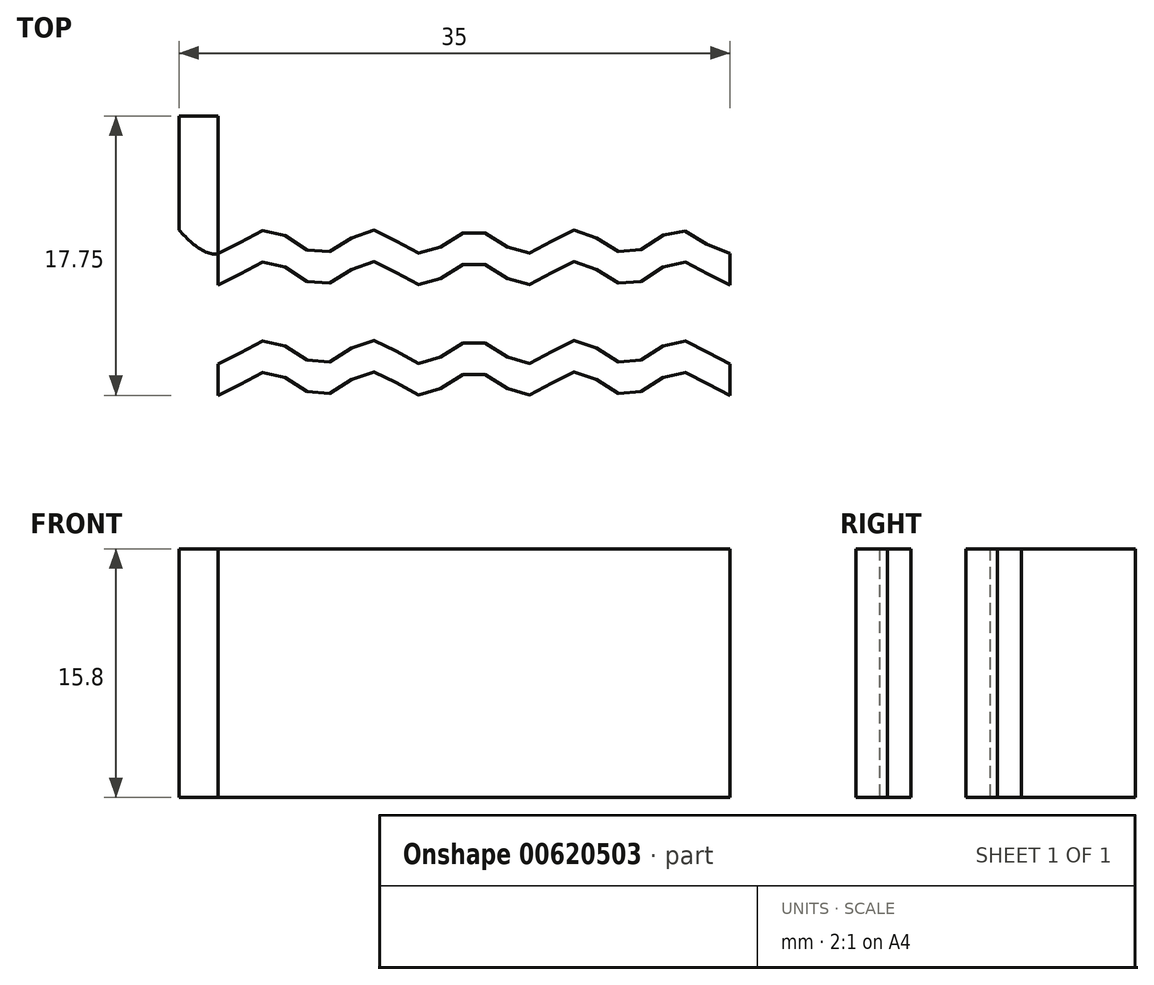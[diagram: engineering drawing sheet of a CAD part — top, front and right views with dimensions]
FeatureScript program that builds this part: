
annotation { "Feature Type Name" : "Feature", "Feature Type Description" : "" }
export const myFeature = defineFeature(function(context is Context, id is Id, definition is map)
    precondition{}
    {
        {
            var Q0;
            Q0=qCreatedBy(makeId("Top.planeOp"),FACE);
            var sketch = newSketch(context, id + "F0", { "sketchPlane" : qUnion([Q0])});
            skLineSegment(sketch, "E0.bottom", {"start": v(-35, 20) * mm, "end": v(-32.5, 20) * mm});
            skLineSegment(sketch, "E0.top", {"start": v(-35, -5) * mm, "end": v(-32.5, -5) * mm});
            skLineSegment(sketch, "E0.left", {"start": v(-35, 20) * mm, "end": v(-35, -5) * mm});
            skLineSegment(sketch, "E0.right", {"start": v(-32.5, 20) * mm, "end": v(-32.5, -5) * mm});
            skArc(sketch, "E1", {"start": v(-32.83, 11.24) * mm, "mid": v(-32.34, 3.76) * mm, "end": v(-32.5, 11.25) * mm, "construction": true});
            skCircle(sketch, "E2", {"center": v(-32.5, 7.5) * mm, "radius": 1.75 * mm, "construction": true});
            skLineSegment(sketch, "E3.bottom", {"start": v(-32.5, 11.25) * mm, "end": v(0, 11.25) * mm, "construction": true});
            skLineSegment(sketch, "E3.top", {"start": v(-32.5, 12.75) * mm, "end": v(0, 12.75) * mm, "construction": true});
            skLineSegment(sketch, "E3.left", {"start": v(-32.5, 11.25) * mm, "end": v(-32.5, 12.75) * mm, "construction": true});
            skLineSegment(sketch, "E3.right", {"start": v(0, 11.25) * mm, "end": v(0, 12.75) * mm, "construction": true});
            skLineSegment(sketch, "E4.bottom", {"start": v(-32.5, 9.25) * mm, "end": v(0, 9.25) * mm, "construction": true});
            skLineSegment(sketch, "E4.top", {"start": v(-32.5, 10.75) * mm, "end": v(0, 10.75) * mm, "construction": true});
            skLineSegment(sketch, "E4.right", {"start": v(0, 9.25) * mm, "end": v(0, 10.75) * mm, "construction": true});
            skLineSegment(sketch, "E5.bottom", {"start": v(-32.5, 5.75) * mm, "end": v(0, 5.75) * mm, "construction": true});
            skLineSegment(sketch, "E5.top", {"start": v(-32.5, 4.25) * mm, "end": v(0, 4.25) * mm, "construction": true});
            skLineSegment(sketch, "E5.left", {"start": v(-32.5, 5.75) * mm, "end": v(-32.5, 4.25) * mm, "construction": true});
            skLineSegment(sketch, "E5.right", {"start": v(0, 5.75) * mm, "end": v(0, 4.25) * mm, "construction": true});
            skLineSegment(sketch, "E6.bottom", {"start": v(-32.5, 3.75) * mm, "end": v(0, 3.75) * mm, "construction": true});
            skLineSegment(sketch, "E6.top", {"start": v(-32.5, 2.25) * mm, "end": v(0, 2.25) * mm, "construction": true});
            skLineSegment(sketch, "E6.left", {"start": v(-32.5, 3.75) * mm, "end": v(-32.5, 2.25) * mm, "construction": true});
            skLineSegment(sketch, "E6.right", {"start": v(0, 3.75) * mm, "end": v(0, 2.25) * mm, "construction": true});
            skPoint(sketch, "E7", {"position": v(-29.25, 12.75) * mm});
            skPoint(sketch, "E8", {"position": v(-26, 12.75) * mm});
            skPoint(sketch, "E9", {"position": v(-22.75, 12.75) * mm});
            skPoint(sketch, "E10", {"position": v(-19.5, 12.75) * mm});
            skPoint(sketch, "E11", {"position": v(-16.25, 12.75) * mm});
            skPoint(sketch, "E12", {"position": v(-13, 12.75) * mm});
            skPoint(sketch, "E13", {"position": v(-9.75, 12.75) * mm});
            skPoint(sketch, "E14", {"position": v(-3.25, 12.75) * mm});
            skPoint(sketch, "E15", {"position": v(-6.5, 12.75) * mm});
            skPoint(sketch, "E16", {"position": v(0, 12.75) * mm});
            skLineSegment(sketch, "E17", {"start": v(-32.5, 12.75) * mm, "end": v(-29.25, 12.75) * mm, "construction": true});
            skLineSegment(sketch, "E18", {"start": v(-29.25, 12.75) * mm, "end": v(-26, 12.75) * mm, "construction": true});
            skLineSegment(sketch, "E19", {"start": v(-26, 12.75) * mm, "end": v(-22.75, 12.75) * mm, "construction": true});
            skLineSegment(sketch, "E20", {"start": v(-22.75, 12.75) * mm, "end": v(-19.5, 12.75) * mm, "construction": true});
            skLineSegment(sketch, "E21", {"start": v(-19.5, 12.75) * mm, "end": v(-16.25, 12.75) * mm, "construction": true});
            skLineSegment(sketch, "E22", {"start": v(-16.25, 12.75) * mm, "end": v(-13, 12.75) * mm, "construction": true});
            skLineSegment(sketch, "E23", {"start": v(-13, 12.75) * mm, "end": v(-9.75, 12.75) * mm, "construction": true});
            skLineSegment(sketch, "E24", {"start": v(-9.75, 12.75) * mm, "end": v(-3.25, 12.75) * mm, "construction": true});
            skLineSegment(sketch, "E25", {"start": v(-6.5, 12.75) * mm, "end": v(-3.25, 12.75) * mm, "construction": true});
            skLineSegment(sketch, "E26", {"start": v(-6.5, 12.75) * mm, "end": v(0, 12.75) * mm, "construction": true});
            skLineSegment(sketch, "E27", {"start": v(-29.25, 12.75) * mm, "end": v(-29.25, 2.25) * mm, "construction": true});
            skLineSegment(sketch, "E28", {"start": v(-26, 12.75) * mm, "end": v(-26, 2.25) * mm, "construction": true});
            skLineSegment(sketch, "E29", {"start": v(-22.75, 12.75) * mm, "end": v(-22.75, 2.25) * mm, "construction": true});
            skLineSegment(sketch, "E30", {"start": v(-19.5, 12.75) * mm, "end": v(-19.5, 2.25) * mm, "construction": true});
            skLineSegment(sketch, "E31", {"start": v(-16.25, 12.75) * mm, "end": v(-16.25, 2.25) * mm, "construction": true});
            skLineSegment(sketch, "E32", {"start": v(-13, 12.75) * mm, "end": v(-13, 2.25) * mm, "construction": true});
            skLineSegment(sketch, "E33", {"start": v(-9.75, 12.75) * mm, "end": v(-9.75, 2.25) * mm, "construction": true});
            skLineSegment(sketch, "E34", {"start": v(-6.5, 12.75) * mm, "end": v(-6.5, 2.25) * mm, "construction": true});
            skFitSpline(sketch, "E35", {"points": [v(-35, 12.75) * mm, v(-32.5, 11.25) * mm, v(-29.25, 12.75) * mm, v(-26, 11.25) * mm, v(-22.75, 12.75) * mm, v(-19.5, 11.25) * mm, v(-16.25, 12.75) * mm, v(-13, 11.25) * mm, v(-9.75, 12.75) * mm, v(-6.5, 11.25) * mm, v(-3.25, 12.75) * mm, v(0, 11.25) * mm, v(2.93, 12.75) * mm, v(2.97, 12.75) * mm], "startDerivative": vector(31.68, -32.9) * mm, "endDerivative": vector(2.76, -1.8) * mm});
            skPoint(sketch, "E36.12.internal.snap0", {"position": v(-16.25, 10.75) * mm});
            skFitSpline(sketch, "E36", {"points": [v(-35, 10.75) * mm, v(-32.5, 9.25) * mm, v(-29.25, 10.75) * mm, v(-26, 9.25) * mm, v(-22.75, 10.75) * mm, v(-19.5, 9.25) * mm, v(-16.25, 10.75) * mm, v(-13, 9.25) * mm, v(-9.75, 10.75) * mm, v(-6.5, 9.25) * mm, v(-3.25, 10.75) * mm, v(0, 9.25) * mm, v(2.97, 10.75) * mm], "startDerivative": vector(31.42, -32.62) * mm, "endDerivative": vector(36, 31.45) * mm});
            skPoint(sketch, "E37.12.internal.snap0", {"position": v(-16.25, 5.75) * mm});
            skFitSpline(sketch, "E37", {"points": [v(-35, 5.75) * mm, v(-32.5, 4.25) * mm, v(-29.25, 5.75) * mm, v(-26, 4.25) * mm, v(-22.75, 5.75) * mm, v(-19.5, 4.25) * mm, v(-16.25, 5.75) * mm, v(-13, 4.25) * mm, v(-9.75, 5.75) * mm, v(-6.5, 4.25) * mm, v(-3.25, 5.75) * mm, v(0, 4.25) * mm, v(2.97, 5.75) * mm], "startDerivative": vector(31.42, -32.62) * mm, "endDerivative": vector(36, 31.45) * mm});
            skPoint(sketch, "E38.12.internal.snap0", {"position": v(-16.25, 3.75) * mm});
            skFitSpline(sketch, "E38", {"points": [v(-35, 3.75) * mm, v(-32.5, 2.25) * mm, v(-29.25, 3.75) * mm, v(-26, 2.25) * mm, v(-22.75, 3.75) * mm, v(-19.5, 2.25) * mm, v(-16.25, 3.75) * mm, v(-13, 2.25) * mm, v(-9.75, 3.75) * mm, v(-6.5, 2.25) * mm, v(-3.25, 3.75) * mm, v(0, 2.25) * mm, v(2.97, 3.75) * mm], "startDerivative": vector(31.42, -32.62) * mm, "endDerivative": vector(36, 31.45) * mm});
            skLineSegment(sketch, "E39", {"start": v(0, 11.25) * mm, "end": v(0, 9.25) * mm});
            skLineSegment(sketch, "E40", {"start": v(0, 4.25) * mm, "end": v(0, 2.25) * mm});
            skSolve(sketch);
        }
        {
            var Q0;
            {var subQ3=sQuery(id+"F0.wireOp",EDGE,"E0.bottom");Q0=makeQuery(id+"F0.imprint","IMPRINT",FACE,{"disambiguationData":[TD([[makeQuery(id+"F0.imprint","IMPRINT",EDGE,{"derivedFrom":subQ3}),-1.0]])]});}
            var Q1;
            {var subQ5=sQuery(id+"F0.wireOp",EDGE,"E39");Q1=makeQuery(id+"F0.imprint","IMPRINT",FACE,{"disambiguationData":[TD([[makeQuery(id+"F0.imprint","IMPRINT",EDGE,{"derivedFrom":subQ5}),-1.0]])]});}
            var Q2;
            {var subQ5=sQuery(id+"F0.wireOp",EDGE,"E40");Q2=makeQuery(id+"F0.imprint","IMPRINT",FACE,{"disambiguationData":[TD([[makeQuery(id+"F0.imprint","IMPRINT",EDGE,{"derivedFrom":subQ5}),-1.0]])]});}
            extrude(context, id + "F1", {"entities" : qUnion([Q0, Q1, Q2]), "endBound" : BoundingType.SYMMETRIC, "depth" : 15.8 * mm, "offsetDistance" : 25 * mm});
        }
    });
